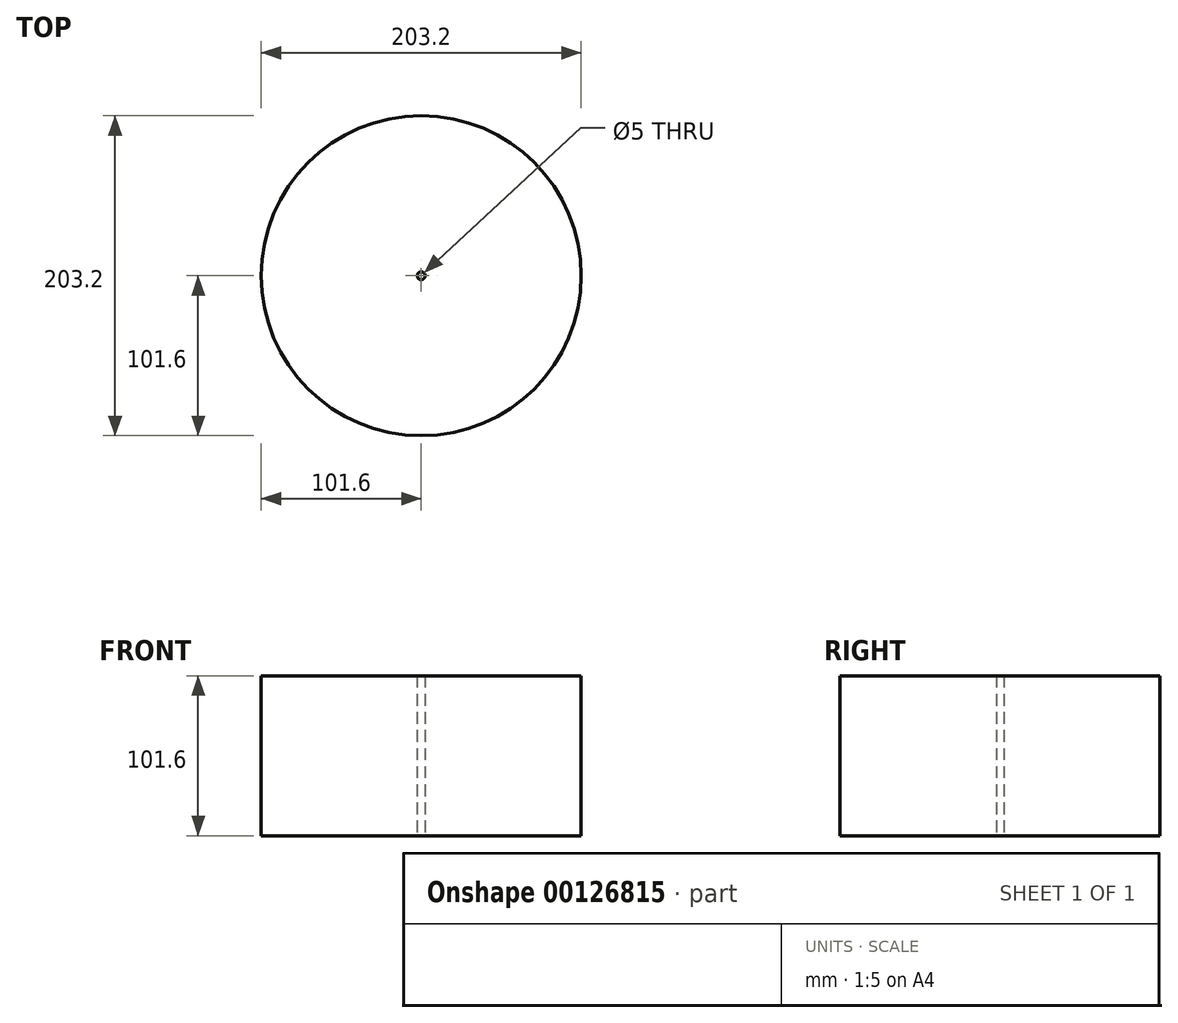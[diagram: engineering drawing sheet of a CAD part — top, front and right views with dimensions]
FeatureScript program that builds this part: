
annotation { "Feature Type Name" : "Feature", "Feature Type Description" : "" }
export const myFeature = defineFeature(function(context is Context, id is Id, definition is map)
    precondition{}
    {
        {
            var Q0;
            Q0=qCreatedBy(makeId("Top.planeOp"),FACE);
            var sketch = newSketch(context, id + "F0", { "sketchPlane" : qUnion([Q0])});
            skCircle(sketch, "E0", {"center": v(0, 0) * mm, "radius": 101.6 * mm});
            skLineSegment(sketch, "E1", {"start": v(0, -101.6) * mm, "end": v(0, 101.6) * mm, "construction": true});
            skLineSegment(sketch, "E2", {"start": v(-101.6, 0) * mm, "end": v(101.6, 0) * mm, "construction": true});
            skLineSegment(sketch, "E3", {"start": v(-65.7, -36.85) * mm, "end": v(0, 0) * mm, "construction": true});
            skLineSegment(sketch, "E4", {"start": v(0, 0) * mm, "end": v(-88.62, -49.7) * mm, "construction": true});
            skLineSegment(sketch, "E5", {"start": v(-88.62, -49.7) * mm, "end": v(88.62, 49.7) * mm, "construction": true});
            skLineSegment(sketch, "E6", {"start": v(-37.25, -65.05) * mm, "end": v(0, 0) * mm, "construction": true});
            skLineSegment(sketch, "E7", {"start": v(0, 0) * mm, "end": v(-50.5, -88.16) * mm, "construction": true});
            skLineSegment(sketch, "E8", {"start": v(-50.5, -88.16) * mm, "end": v(50.5, 88.16) * mm, "construction": true});
            skLineSegment(sketch, "E9", {"start": v(0, 0) * mm, "end": v(38.52, -64.45) * mm, "construction": true});
            skLineSegment(sketch, "E10", {"start": v(0, 0) * mm, "end": v(52.13, -87.2) * mm, "construction": true});
            skLineSegment(sketch, "E11", {"start": v(52.13, -87.2) * mm, "end": v(-52.13, 87.2) * mm, "construction": true});
            skLineSegment(sketch, "E12", {"start": v(66.14, -36.73) * mm, "end": v(0, 0) * mm, "construction": true});
            skLineSegment(sketch, "E13", {"start": v(0, 0) * mm, "end": v(88.82, -49.32) * mm, "construction": true});
            skLineSegment(sketch, "E14", {"start": v(88.82, -49.32) * mm, "end": v(-87.5, 51.65) * mm, "construction": true});
            skCircle(sketch, "E15", {"center": v(0, 0) * mm, "radius": 76.2 * mm, "construction": true});
            skPoint(sketch, "E16", {"position": v(0, 76.2) * mm});
            skPoint(sketch, "E17", {"position": v(37.87, 66.12) * mm});
            skPoint(sketch, "E18", {"position": v(66.46, 37.27) * mm});
            skPoint(sketch, "E19", {"position": v(76.2, 0) * mm});
            skPoint(sketch, "E20", {"position": v(66.14, -36.73) * mm});
            skPoint(sketch, "E21", {"position": v(38.52, -64.45) * mm});
            skPoint(sketch, "E22", {"position": v(0, -76.2) * mm});
            skPoint(sketch, "E23", {"position": v(-37.25, -65.05) * mm});
            skPoint(sketch, "E24", {"position": v(-65.7, -36.85) * mm});
            skPoint(sketch, "E25", {"position": v(-76.2, 0) * mm});
            skPoint(sketch, "E26", {"position": v(-65.45, 39.03) * mm});
            skPoint(sketch, "E27", {"position": v(-39.1, 65.4) * mm});
            skSolve(sketch);
        }
        {
            var Q0;
            Q0=makeQuery(id+"F0.imprint","IMPRINT",FACE,{"disambiguationData":[TD([[makeQuery(id+"F0.imprint","IMPRINT",EDGE,{"derivedFrom":sQuery(id+"F0.wireOp",EDGE,"E0")}),1.0]])]});
            extrude(context, id + "F1", {"entities" : qUnion([Q0]), "depth" : 101.6 * mm});
        }
        {
            var Q0;
            Q0=sQuery(id+"F0.wireOp",VERTEX,"E12.end");
            var Q1;
            Q1=makeQuery(id+"F1.opExtrude","SWEPT_BODY",BODY,{"disambiguationData":[OSD([sQuery(id+"F0.wireOp",EDGE,"E0")])]});
            hole(context, id + "F2", {"style" : HoleStyle.SIMPLE, "endStyle" : HoleEndStyle.THROUGH, "oppositeDirection" : true, "holeDiameter" : 5 * mm, "locations" : qUnion([Q0]), "scope" : qUnion([Q1]), "isTappedThrough" : true});
        }
    });
